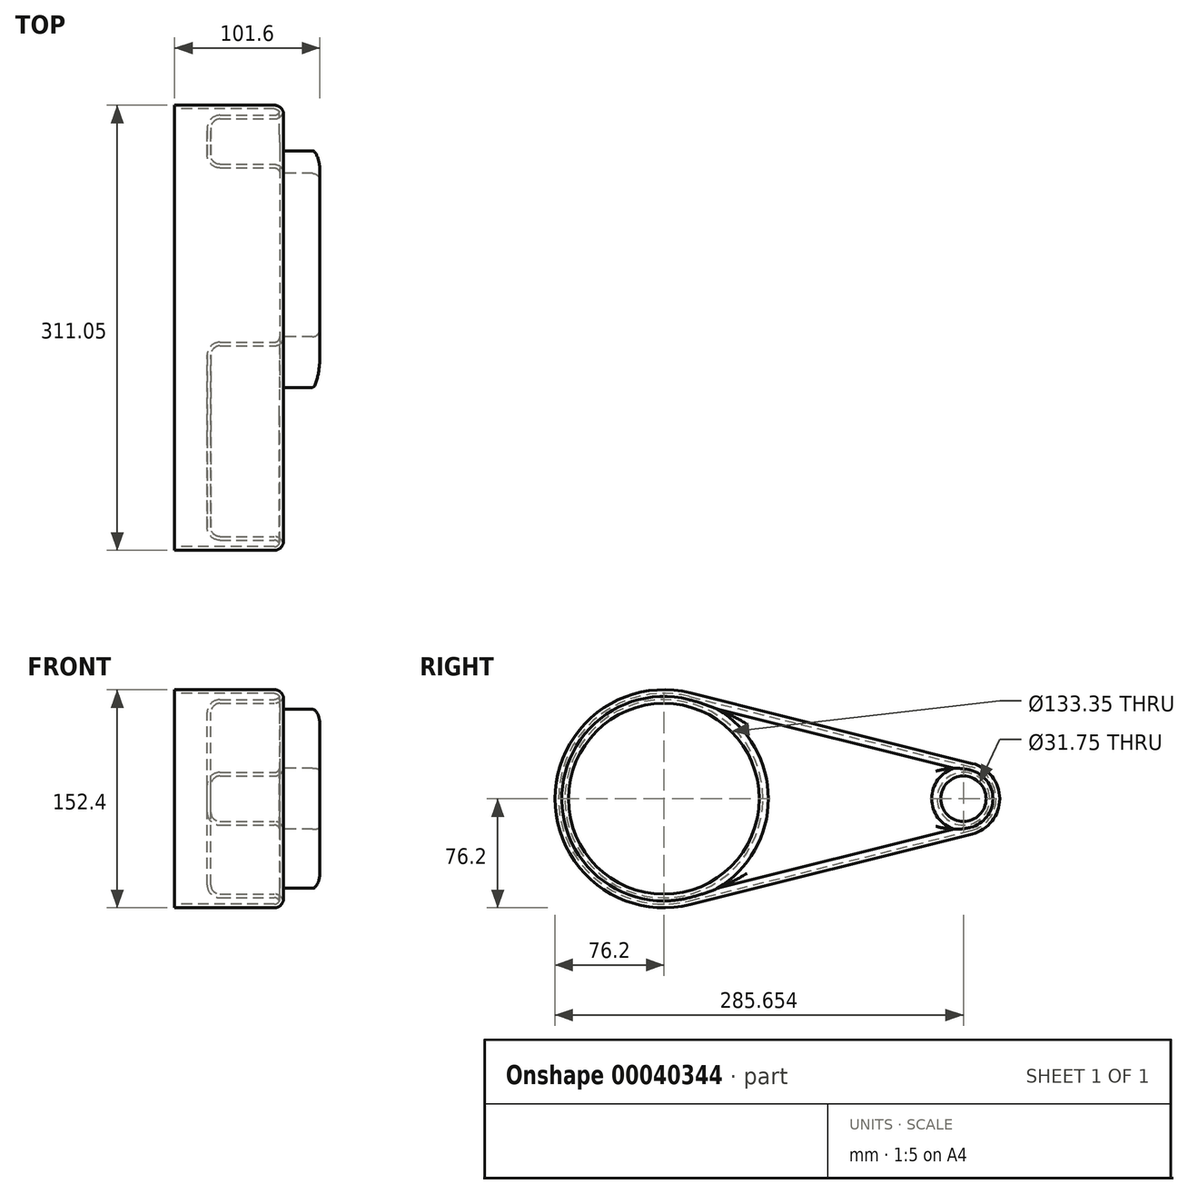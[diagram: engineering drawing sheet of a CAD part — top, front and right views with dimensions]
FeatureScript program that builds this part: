
annotation { "Feature Type Name" : "Feature", "Feature Type Description" : "" }
export const myFeature = defineFeature(function(context is Context, id is Id, definition is map)
    precondition{}
    {
        {
            var Q0;
            Q0=qCreatedBy(makeId("Right.planeOp"),FACE);
            var sketch = newSketch(context, id + "F0", { "sketchPlane" : qUnion([Q0])});
            skCircle(sketch, "E0", {"center": v(0, 0) * mm, "radius": 76.2 * mm});
            skCircle(sketch, "E1", {"center": v(209.45, 0) * mm, "radius": 25.4 * mm});
            skLineSegment(sketch, "E2", {"start": v(18.48, 73.92) * mm, "end": v(215.61, 24.64) * mm});
            skLineSegment(sketch, "E3", {"start": v(18.48, -73.92) * mm, "end": v(215.61, -24.64) * mm});
            skSolve(sketch);
        }
        {
            var Q0;
            {var subQ0=sQuery(id+"F0.wireOp",EDGE,"E0");var subQ2=makeQuery(id+"F0.imprint","INTERSECT",VERTEX,{"derivedFrom":[subQ0,sQuery(id+"F0.wireOp",EDGE,"E2")]});Q0=makeQuery(id+"F0.imprint","IMPRINT",FACE,{"disambiguationData":[TD([[makeQuery(id+"F0.imprint","IMPRINT",EDGE,{"disambiguationData":[TD([[subQ2,-1.0]])],"derivedFrom":subQ0}),1.0]])]});}
            var Q1;
            {var subQ1=sQuery(id+"F0.wireOp",EDGE,"E2");Q1=makeQuery(id+"F0.imprint","IMPRINT",FACE,{"disambiguationData":[TD([[makeQuery(id+"F0.imprint","IMPRINT",EDGE,{"derivedFrom":subQ1}),-1.0]])]});}
            var Q2;
            {var subQ0=sQuery(id+"F0.wireOp",EDGE,"E1");var subQ2=makeQuery(id+"F0.imprint","INTERSECT",VERTEX,{"derivedFrom":[subQ0,sQuery(id+"F0.wireOp",EDGE,"E2")]});Q2=makeQuery(id+"F0.imprint","IMPRINT",FACE,{"disambiguationData":[TD([[makeQuery(id+"F0.imprint","IMPRINT",EDGE,{"disambiguationData":[TD([[subQ2,-1.0]])],"derivedFrom":subQ0}),1.0]])]});}
            extrude(context, id + "F1", {"entities" : qUnion([Q0, Q1, Q2]), "depth" : 76.2 * mm});
        }
        {
            var Q0;
            Q0=makeQuery(id+"F1.opExtrude","CAP_FACE",FACE,{"disambiguationData":[OSD([sQuery(id+"F0.wireOp",EDGE,"E0"),sQuery(id+"F0.wireOp",EDGE,"E1"),sQuery(id+"F0.wireOp",EDGE,"E2"),sQuery(id+"F0.wireOp",EDGE,"E3")])],"isStart":false});
            var sketch = newSketch(context, id + "F2", { "sketchPlane" : qUnion([Q0])});
            skCircle(sketch, "E4", {"center": v(209.45, 0) * mm, "radius": 15.88 * mm});
            skCircle(sketch, "E5", {"center": v(0, 0) * mm, "radius": 66.68 * mm});
            skSolve(sketch);
        }
        {
            var Q0;
            Q0 = qSketchRegion(id + "F2", true);
            extrude(context, id + "F3", {"entities" : qUnion([Q0]), "operationType" : NewBodyOperationType.REMOVE, "oppositeDirection" : true, "depth" : 50.8 * mm});
        }
        {
            var Q0;
            Q0=makeQuery(id+"F1.opExtrude","CAP_FACE",FACE,{"disambiguationData":[OSD([sQuery(id+"F0.wireOp",EDGE,"E0"),sQuery(id+"F0.wireOp",EDGE,"E1"),sQuery(id+"F0.wireOp",EDGE,"E2"),sQuery(id+"F0.wireOp",EDGE,"E3")])],"isStart":false});
            var Q1;
            Q1=makeQuery(id+"F3.boolean.opBoolean","COPY",EDGE,{"derivedFrom":makeQuery(id+"F3.opExtrude","CAP_EDGE",EDGE,{"disambiguationData":[OSD([sQuery(id+"F2.wireOp",EDGE,"E5")])],"isStart":false})});
            var Q2;
            Q2=makeQuery(id+"F3.boolean.opBoolean","COPY",EDGE,{"derivedFrom":makeQuery(id+"F3.opExtrude","CAP_EDGE",EDGE,{"disambiguationData":[OSD([sQuery(id+"F2.wireOp",EDGE,"E4")])],"isStart":false})});
            fillet(context, id + "F4", {"entities" : qUnion([Q0, Q1, Q2]), "radius" : 6.35 * mm, "tangentPropagation" : true, "allowEdgeOverflow" : false});
        }
        {
            var Q0;
            Q0=makeQuery(id+"F1.opExtrude","CAP_FACE",FACE,{"disambiguationData":[OSD([sQuery(id+"F0.wireOp",EDGE,"E0"),sQuery(id+"F0.wireOp",EDGE,"E1"),sQuery(id+"F0.wireOp",EDGE,"E2"),sQuery(id+"F0.wireOp",EDGE,"E3")])],"isStart":true});
            shell(context, id + "F5", {"entities" : qUnion([Q0]), "thickness" : 2.54 * mm});
        }
        {
            var Q0;
            Q0=makeQuery(id+"F1.opExtrude","CAP_FACE",FACE,{"disambiguationData":[OSD([sQuery(id+"F0.wireOp",EDGE,"E0"),sQuery(id+"F0.wireOp",EDGE,"E1"),sQuery(id+"F0.wireOp",EDGE,"E2"),sQuery(id+"F0.wireOp",EDGE,"E3")])],"isStart":false});
            extrude(context, id + "F6", {"entities" : qUnion([Q0]), "operationType" : NewBodyOperationType.ADD, "depth" : 25.4 * mm});
        }
        {
            var Q0;
            Q0=makeQuery(id+"F6.opExtrude","CAP_FACE",FACE,{"disambiguationData":[OSD([sQuery(id+"F0.wireOp",EDGE,"E0"),sQuery(id+"F0.wireOp",EDGE,"E1"),sQuery(id+"F0.wireOp",EDGE,"E2"),sQuery(id+"F0.wireOp",EDGE,"E3")])],"isStart":false});
            fillet(context, id + "F7", {"entities" : qUnion([Q0]), "radius" : 5.08 * mm, "tangentPropagation" : true, "allowEdgeOverflow" : false});
        }
    });
